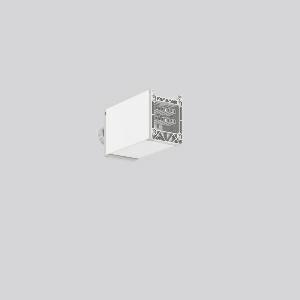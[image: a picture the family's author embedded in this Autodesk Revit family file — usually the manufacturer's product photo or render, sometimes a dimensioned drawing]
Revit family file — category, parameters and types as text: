
# Revit family: linedo_anfangseinspeisung_982859_002_f26b
name_source: partatom
category: Lighting Fixtures
units: mm (PartAtom-declared; Revit-internal decimal feet)

## family parameters
Cut with Voids When Loaded = No
Host = Face
Light Source = No
Part Type = Normal
Room Calculation Point = No
Round Connector Dimension = Use Diameter
Shared = No

## types (1)
- LINEDO Anfangseinspeisung
    Apparent Load = 0 VA
    Default Elevation = 1800 mm
    Description = Series: LINEDO
Initial power feed (short Version), 7-pole, connection socket. Housing: extruded aluminium profile, powder-coated. Cover made of plastic, surface like housing. LINEDO plug system, plastic, light grey. 1 cable gland (M25). Cable gland on side or on top. Convenient connection with flat connector.
Colour: white
Length: 134 mm
Width: 58 mm
Height: 76 mm
Weight: 278 g
    Height = 76 mm
    Lamp = 0 x
    Length = 134 mm
    Luminous efficacy = 0 lm/W
    Manufacturer = RZB
    ModVariant = No
    Model = 982859.002
    Mounting Place = Ceiling
    Mounting Type = Surface mounted
    Number of Poles = 1
    OnlyDefault = Yes
    Power Factor = 1
    Product Name = LINEDO Anfangseinspeisung
    Product group = Surface mounted continuous line luminaire system
    ProductGroupID = 310
    Protection Class = Protection class I
    Protection Degree = Degree of protection
    RLX_Detail_Level = 1
    RLX_Emergency_Light_Flux = 0 lm
    RLX_Emergency_Type = 0
    RLX_Emergency_Type_DB = No
    RlxData = <blob elided: 12853 chars, md5=3361b130>
    Standby Power = 0 W
    System Light Flux = 0 lm
    System Power = 0 W
    Type Comments = Product without accessories
    Type Image = 982859.002.jpg
    URL = http://relux.com
    VarID = ---
    Voltage = 0 V
    Weight = 0.00 kg
    Width = 58 mm

## geometry (parser evidence)
native form markers: Sweep x9
no freeform markers — native parametric forms only
